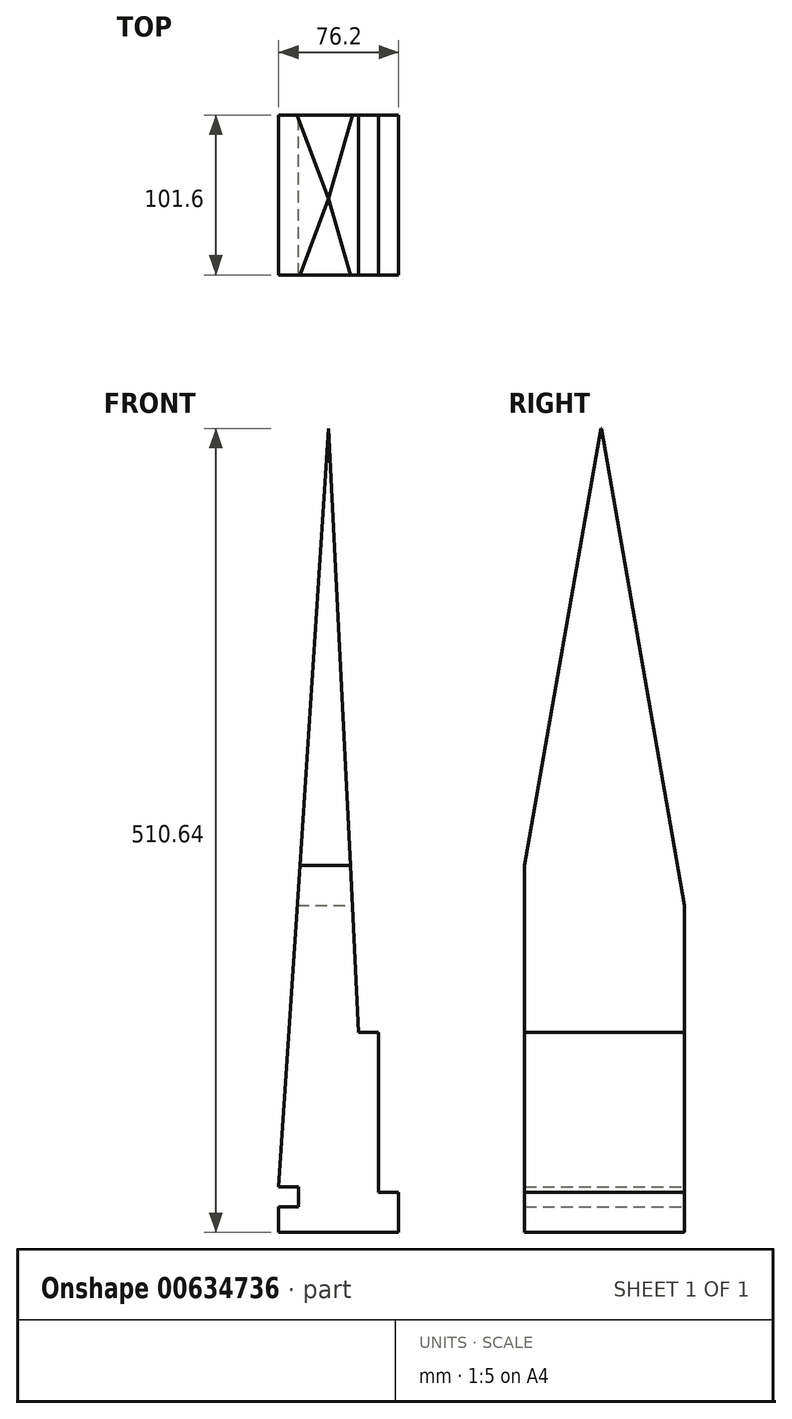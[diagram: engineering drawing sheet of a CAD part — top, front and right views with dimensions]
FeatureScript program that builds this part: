
annotation { "Feature Type Name" : "Feature", "Feature Type Description" : "" }
export const myFeature = defineFeature(function(context is Context, id is Id, definition is map)
    precondition{}
    {
        {
            var Q0;
            Q0=qCreatedBy(makeId("Front.planeOp"),FACE);
            var sketch = newSketch(context, id + "F0", { "sketchPlane" : qUnion([Q0])});
            skLineSegment(sketch, "E0", {"start": v(0, 42.36) * mm, "end": v(0, 40.24) * mm});
            skLineSegment(sketch, "E1", {"start": v(0, 0) * mm, "end": v(76.2, 0) * mm});
            skLineSegment(sketch, "E2", {"start": v(76.2, 0) * mm, "end": v(76.2, 25.4) * mm});
            skLineSegment(sketch, "E3", {"start": v(76.2, 25.4) * mm, "end": v(63.5, 25.4) * mm});
            skLineSegment(sketch, "E4", {"start": v(63.5, 25.4) * mm, "end": v(63.5, 127) * mm});
            skLineSegment(sketch, "E5", {"start": v(63.5, 127) * mm, "end": v(50.8, 127) * mm});
            skLineSegment(sketch, "E6", {"start": v(50.8, 127) * mm, "end": v(31.6, 510.64) * mm});
            skLineSegment(sketch, "E7", {"start": v(31.6, 510.64) * mm, "end": v(0, 29.08) * mm});
            skLineSegment(sketch, "E8", {"start": v(0, 29.08) * mm, "end": v(12.7, 29.08) * mm});
            skLineSegment(sketch, "E9", {"start": v(12.7, 29.08) * mm, "end": v(12.7, 16.38) * mm});
            skLineSegment(sketch, "E10", {"start": v(12.7, 16.38) * mm, "end": v(0, 16.38) * mm});
            skLineSegment(sketch, "E11", {"start": v(0, 16.38) * mm, "end": v(0, 0) * mm});
            skSolve(sketch);
        }
        {
            var Q0;
            Q0 = qSketchRegion(id + "F0", true);
            extrude(context, id + "F1", {"entities" : qUnion([Q0]), "depth" : 76.2 * mm, "offsetDistance" : 25.4 * mm});
        }
        {
            var Q0;
            Q0 = qSketchRegion(id + "F0", true);
            var Q1;
            Q1=makeQuery(id+"F1.opExtrude","CAP_FACE",FACE,{"disambiguationData":[OSD([sQuery(id+"F0.wireOp",EDGE,"E1"),sQuery(id+"F0.wireOp",EDGE,"E2"),sQuery(id+"F0.wireOp",EDGE,"E3"),sQuery(id+"F0.wireOp",EDGE,"E4"),sQuery(id+"F0.wireOp",EDGE,"E5"),sQuery(id+"F0.wireOp",EDGE,"E6"),sQuery(id+"F0.wireOp",EDGE,"E7"),sQuery(id+"F0.wireOp",EDGE,"E8"),sQuery(id+"F0.wireOp",EDGE,"E9"),sQuery(id+"F0.wireOp",EDGE,"E10"),sQuery(id+"F0.wireOp",EDGE,"E11")])],"isStart":false});
            extrude(context, id + "F2", {"entities" : qUnion([Q0, Q1]), "operationType" : NewBodyOperationType.ADD, "depth" : 25.4 * mm, "offsetDistance" : 25.4 * mm});
        }
        {
            var Q0;
            Q0=qCreatedBy(makeId("Right.planeOp"),FACE);
            var sketch = newSketch(context, id + "F3", { "sketchPlane" : qUnion([Q0])});
            skLineSegment(sketch, "E12.bottom", {"start": v(36.27, 0) * mm, "end": v(-142.3, 0) * mm, "construction": true});
            skLineSegment(sketch, "E12.left", {"start": v(36.27, 0) * mm, "end": v(28.63, 603.81) * mm});
            skLineSegment(sketch, "E12.right", {"start": v(-142.3, 0) * mm, "end": v(-150.9, 678.91) * mm});
            skLineSegment(sketch, "E13", {"start": v(-142.3, 0) * mm, "end": v(-53.02, 511) * mm});
            skLineSegment(sketch, "E14", {"start": v(-53.02, 511) * mm, "end": v(36.27, 0) * mm});
            skLineSegment(sketch, "E15", {"start": v(-150.9, 678.91) * mm, "end": v(28.63, 603.81) * mm});
            skSolve(sketch);
        }
        {
            var Q0;
            Q0=makeQuery(id+"F3.imprint","IMPRINT",FACE,{"disambiguationData":[TD([[makeQuery(id+"F3.imprint","IMPRINT",EDGE,{"derivedFrom":sQuery(id+"F3.wireOp",EDGE,"E12.left")}),1.0]])]});
            extrude(context, id + "F4", {"entities" : qUnion([Q0]), "operationType" : NewBodyOperationType.REMOVE, "endBound" : BoundingType.SYMMETRIC, "oppositeDirection" : true, "depth" : 254 * mm, "offsetDistance" : 25.4 * mm});
        }
    });
